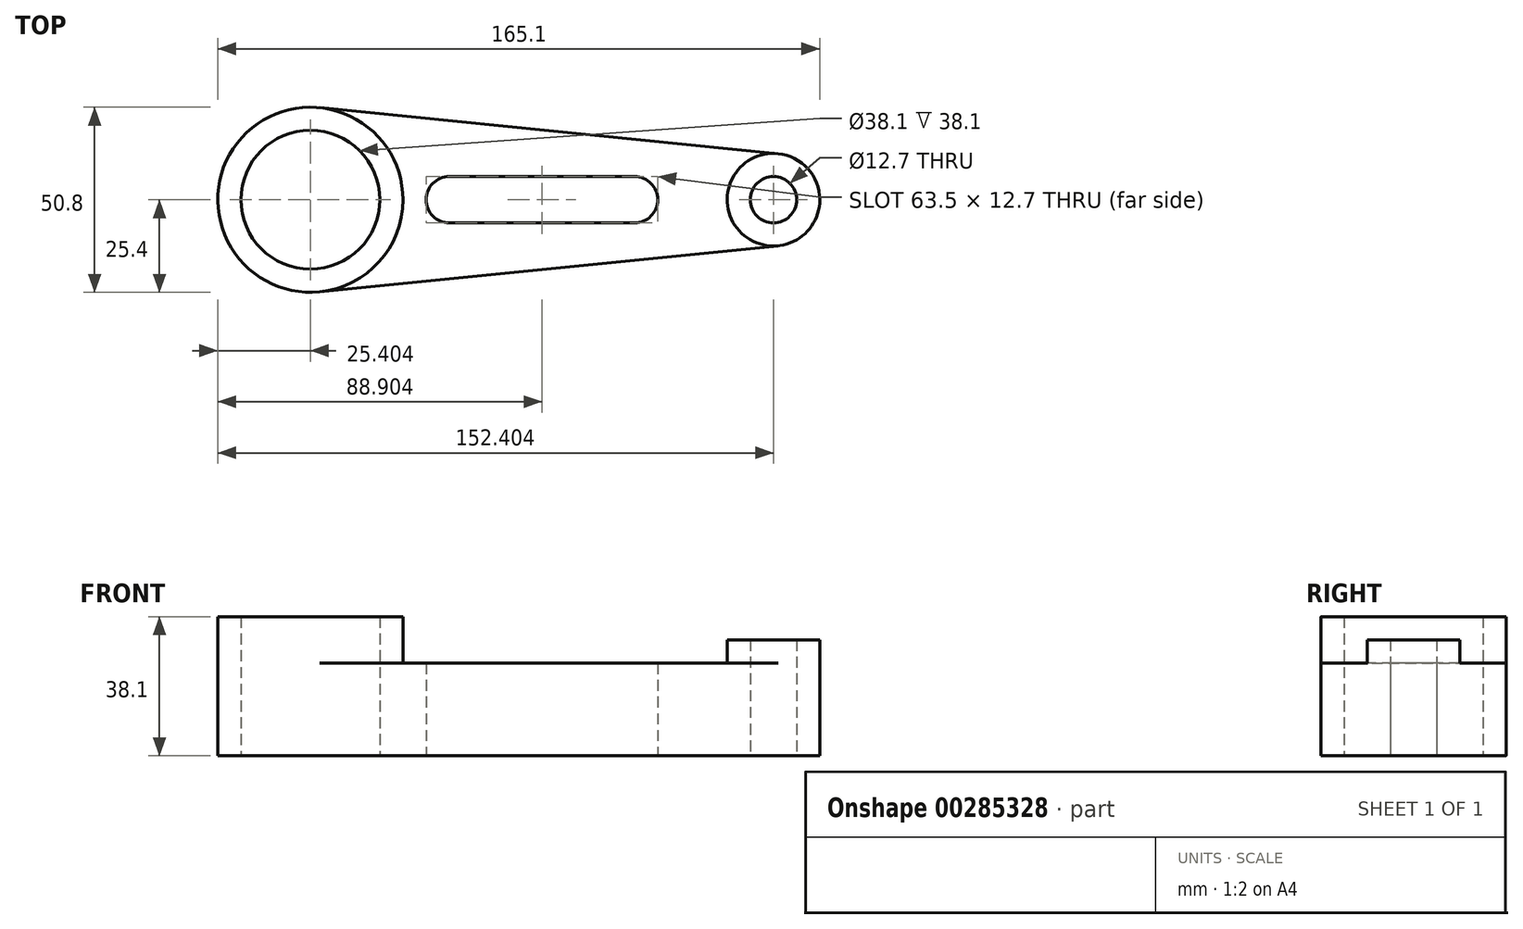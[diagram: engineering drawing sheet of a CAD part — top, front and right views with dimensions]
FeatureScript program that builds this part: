
annotation { "Feature Type Name" : "Feature", "Feature Type Description" : "" }
export const myFeature = defineFeature(function(context is Context, id is Id, definition is map)
    precondition{}
    {
        {
            var Q0;
            Q0=qCreatedBy(makeId("Top.planeOp"),FACE);
            var sketch = newSketch(context, id + "F0", { "sketchPlane" : qUnion([Q0])});
            skCircle(sketch, "E0", {"center": v(-52.03, 0) * mm, "radius": 19.05 * mm});
            skCircle(sketch, "E1", {"center": v(-52.03, 0) * mm, "radius": 25.4 * mm});
            skCircle(sketch, "E2", {"center": v(74.97, 0) * mm, "radius": 6.35 * mm});
            skCircle(sketch, "E3", {"center": v(74.97, 0) * mm, "radius": 12.7 * mm});
            skArc(sketch, "E4", {"start": v(36.87, -6.35) * mm, "mid": v(43.22, 0) * mm, "end": v(36.87, 6.35) * mm});
            skArc(sketch, "E5", {"start": v(-13.93, 6.35) * mm, "mid": v(-20.28, 0) * mm, "end": v(-13.93, -6.35) * mm});
            skPoint(sketch, "E6", {"position": v(-13.93, 6.35) * mm});
            skPoint(sketch, "E7", {"position": v(-13.93, -6.35) * mm});
            skPoint(sketch, "E8", {"position": v(36.87, 6.35) * mm});
            skPoint(sketch, "E9", {"position": v(36.87, -6.35) * mm});
            skLineSegment(sketch, "E10", {"start": v(-13.93, 6.35) * mm, "end": v(36.87, 6.35) * mm});
            skLineSegment(sketch, "E11", {"start": v(-13.93, -6.35) * mm, "end": v(36.87, -6.35) * mm});
            skLineSegment(sketch, "E12", {"start": v(-49.49, 25.27) * mm, "end": v(76.24, 12.64) * mm});
            skLineSegment(sketch, "E13", {"start": v(-49.49, -25.27) * mm, "end": v(76.24, -12.64) * mm});
            skSolve(sketch);
        }
        {
            var Q0;
            Q0=makeQuery(id+"F0.imprint","IMPRINT",FACE,{"disambiguationData":[TD([[makeQuery(id+"F0.imprint","IMPRINT",EDGE,{"derivedFrom":sQuery(id+"F0.wireOp",EDGE,"E4")}),-1.0]])]});
            extrude(context, id + "F1", {"entities" : qUnion([Q0]), "depth" : 25.4 * mm});
        }
        {
            var Q0;
            Q0=makeQuery(id+"F0.imprint","IMPRINT",FACE,{"disambiguationData":[TD([[makeQuery(id+"F0.imprint","IMPRINT",EDGE,{"derivedFrom":sQuery(id+"F0.wireOp",EDGE,"E0")}),-1.0]])]});
            extrude(context, id + "F2", {"entities" : qUnion([Q0]), "operationType" : NewBodyOperationType.ADD, "depth" : 38.1 * mm});
        }
        {
            var Q0;
            Q0=makeQuery(id+"F0.imprint","IMPRINT",FACE,{"disambiguationData":[TD([[makeQuery(id+"F0.imprint","IMPRINT",EDGE,{"derivedFrom":sQuery(id+"F0.wireOp",EDGE,"E2")}),-1.0]])]});
            extrude(context, id + "F3", {"entities" : qUnion([Q0]), "operationType" : NewBodyOperationType.ADD, "depth" : 31.75 * mm});
        }
    });
